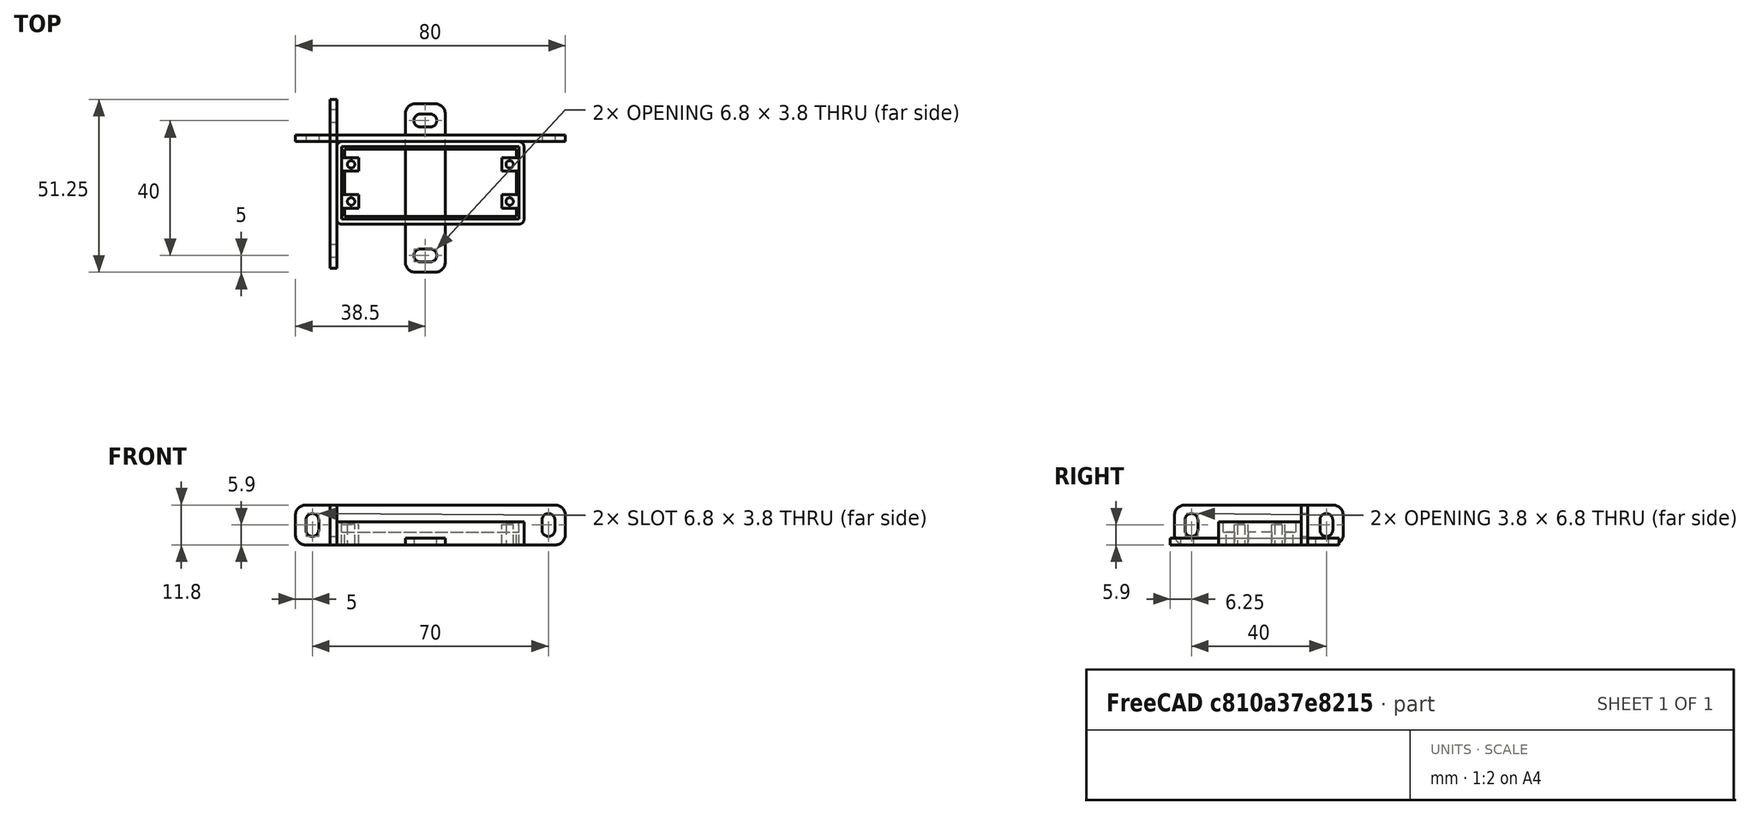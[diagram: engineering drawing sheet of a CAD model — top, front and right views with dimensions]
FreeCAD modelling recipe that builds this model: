
FCSTD DOCUMENT  (FreeCAD 0.21R33694 (Git))
Label: rp2040
License: All rights reserved
LicenseURL: http://en.wikipedia.org/wiki/All_rights_reserved
objects: Part::Box×4, Part::MultiFuse×3, Part::Feature×3, Part::FeaturePython×2, Part::Cut×2, Spreadsheet::Sheet×1, Part::Cylinder×1, Part::Fillet×1, App::Part×1
note: 16 computed .brp shape members not serialized (recipe doc carries the construction recipe); baked Part::Feature solids carry a one-line shape summary decoded from their .brp

FEATURE [Spreadsheet::Sheet] Spreadsheet  label="p"
  cells = A1='hole_x_dist; B1(hole_x_dist)=47; A2='hole_y_dist; B2(hole_y_dist)=11; A3='pcb_under; B3(pcb_under)=3; A4='pcb_x; B4(pcb_x)=52.5; A5='pcb_y; B5(pcb_y)=21.5; A6='hole_stand_x; B6(hole_stand_x)=5; A7='hole_stand_x_offset; B7(hole_stand_x_offset)=0; A8='hole_stand_y; B8(hole_stand_y)=4; A9='hole_stand_y_offset; B9(hole_stand_y_offset)=3.25; A10='hole_r; B10(hole_r)=1.1; A11='box_wall; B11(box_wall)=1.5; A12='under_layer; B12(under_layer)=3; A13='pcb_height; B13(pcb_height)=0.8; A14='under_pcb_border; B14(under_pcb_border)=0.8
FEATURE [Part::Box] Box  label="bottom cube"
  AttacherType = Attacher::AttachEngine3D
  Height = 6.8
  Length = 55.5
  Width = 24.5
  expr: Height = <<p>>.pcb_under + <<p>>.pcb_height + <<p>>.under_layer
  expr: Length = <<p>>.pcb_x + <<p>>.box_wall * 2
  expr: Width = <<p>>.pcb_y + <<p>>.box_wall * 2
FEATURE [Part::Box] Box001  label="bottom extraction"
  AttacherType = Attacher::AttachEngine3D
  Height = 10
  Length = 50.9
  Placement = pos=(2.3,2.3,0) rot=(0,0,1;0rad)
  Width = 19.9
  expr: .Placement.Base.x = <<p>>.under_pcb_border + <<p>>.box_wall
  expr: .Placement.Base.y = <<p>>.under_pcb_border + <<p>>.box_wall
  expr: Length = <<p>>.pcb_x - <<p>>.under_pcb_border * 2
  expr: Width = <<p>>.pcb_y - <<p>>.under_pcb_border * 2
FEATURE [Part::Box] Box002  label="pcb extraction"
  AttacherType = Attacher::AttachEngine3D
  Height = 10
  Length = 52.5
  Placement = pos=(1.5,1.5,3.8) rot=(0,0,1;0rad)
  Width = 21.5
  expr: .Placement.Base.x = <<p>>.box_wall
  expr: .Placement.Base.y = <<p>>.box_wall
  expr: .Placement.Base.z = <<p>>.under_pcb_border + <<p>>.under_layer
  expr: Length = <<p>>.pcb_x
  expr: Width = <<p>>.pcb_y
FEATURE [Part::MultiFuse] Fusion  label="bottom extraction001"
  Shapes = -> [Box001,Box002]
FEATURE [Part::Box] Box003  label="hole stand cube"
  AttacherType = Attacher::AttachEngine3D
  Height = 6
  Length = 5
  Placement = pos=(1.5,4.75,0) rot=(0,0,1;0rad)
  Width = 4
  expr: .Placement.Base.x = <<p>>.box_wall + <<p>>.hole_stand_x_offset
  expr: .Placement.Base.y = <<p>>.box_wall + <<p>>.hole_stand_y_offset
  expr: Height = <<p>>.pcb_under + <<p>>.under_layer
  expr: Length = <<p>>.hole_stand_x
  expr: Width = <<p>>.hole_stand_y
FEATURE [Part::FeaturePython] Array  label="hole stand array"  # Draft array (typed FeaturePython)
  Angle = 360
  ArrayType = 0
  Axis = (0,0,1)
  Base = -> Box003
  Center = (0,0,0)
  Count = 4
  Fuse = false
  IntervalAxis = (0,0,0)
  IntervalX = (47.5,0,0)
  IntervalY = (0,11,0)
  IntervalZ = (0,0,1)
  NumberPolar = 1
  NumberX = 2
  NumberY = 2
  NumberZ = 1
  expr: .IntervalX.x = <<p>>.pcb_x - <<p>>.hole_stand_x - 2 * <<p>>.hole_stand_x_offset
  expr: .IntervalY.y = <<p>>.pcb_y - <<p>>.hole_stand_y - 2 * <<p>>.hole_stand_y_offset
FEATURE [Part::Cylinder] Cylinder  label="pcb hole"
  Angle = 360
  AttacherType = Attacher::AttachEngine3D
  FirstAngle = 0
  Height = 10
  Placement = pos=(4.25,6.75,0) rot=(0,0,1;0rad)
  Radius = 1.1
  SecondAngle = 0
  expr: .Placement.Base.x = (<<p>>.box_wall * 2 + <<p>>.pcb_x - <<p>>.hole_x_dist) / 2
  expr: .Placement.Base.y = (<<p>>.box_wall * 2 + <<p>>.pcb_y - <<p>>.hole_y_dist) / 2
  expr: Radius = <<p>>.hole_r
FEATURE [Part::FeaturePython] Array001  label="hole array"  # Draft array (typed FeaturePython)
  Angle = 360
  ArrayType = 0
  Axis = (0,0,1)
  Base = -> Cylinder
  Center = (0,0,0)
  Count = 4
  Fuse = false
  IntervalAxis = (0,0,0)
  IntervalX = (47,0,0)
  IntervalY = (0,11,0)
  IntervalZ = (0,0,1)
  NumberPolar = 1
  NumberX = 2
  NumberY = 2
  NumberZ = 1
  expr: .IntervalX.x = <<p>>.hole_x_dist
  expr: .IntervalY.y = <<p>>.hole_y_dist
FEATURE [Part::Fillet] Fillet001  label="bottom cube fillet"
  Base = -> Box
  Edges = 4 edges r=1.5: [Edge1,Edge3,Edge5,Edge7]
FEATURE [Part::Feature] Body003  label="attach plane y rotated dir001"
  Placement = pos=(0,-13,0) rot=(0,-1,0;1.5708rad)
  shape: bbox 2 x 50 x 11.8 mm, 20 faces (baked)
FEATURE [Part::Feature] Cut004  label="attach plane y dir001"
  Placement = pos=(20.35,-14.25,0) rot=(0,0,1;0rad)
  shape: bbox 11.8 x 50 x 2 mm, 20 faces (baked)
FEATURE [Part::Feature] Body006  label="attach plane x reverse rotated dir001"
  Placement = pos=(-12.25,26.5,0) rot=(1,0,0;1.5708rad)
  shape: bbox 80 x 2 x 11.8 mm, 18 faces (baked)
FEATURE [Part::MultiFuse] Fusion002  label="bottom fusion"
  Shapes = -> [Fillet001,Body006]
FEATURE [Part::Cut] Cut  label="pcb box cut"
  Base = -> Fusion002
  Tool = -> Fusion
FEATURE [Part::MultiFuse] Fusion001  label="frame fusion"
  Shapes = -> [Array,Cut]
FEATURE [Part::Cut] Cut001  label="frame fusion with holes"
  Base = -> Fusion001
  Tool = -> Array001
FEATURE [App::Part] Part  label="pcb with 4 holes part"
  Group = -> [Fusion,Fusion002,Box002,Box003,Box001,Array001,Cut,Array,Cylinder,Fusion001,Cut001]
  Origin = -> Origin
